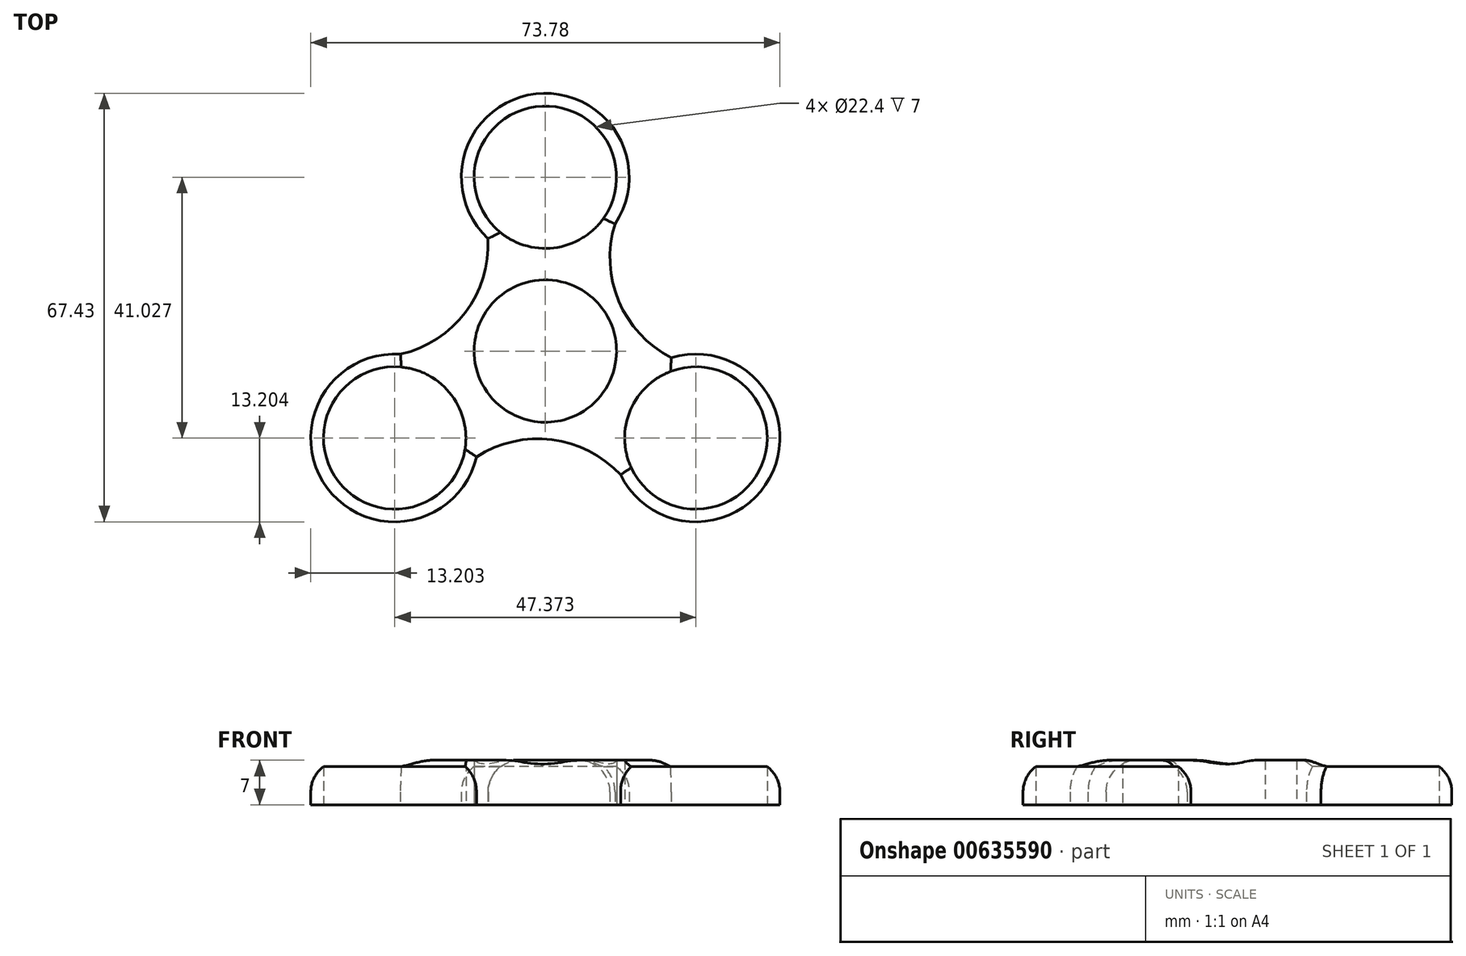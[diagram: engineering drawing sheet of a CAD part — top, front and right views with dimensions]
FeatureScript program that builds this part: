
annotation { "Feature Type Name" : "Feature", "Feature Type Description" : "" }
export const myFeature = defineFeature(function(context is Context, id is Id, definition is map)
    precondition{}
    {
        {
            var Q0;
            Q0=qCreatedBy(makeId("Top.planeOp"),FACE);
            var sketch = newSketch(context, id + "F0", { "sketchPlane" : qUnion([Q0])});
            skCircle(sketch, "E0", {"center": v(0, 0) * mm, "radius": 11.2 * mm});
            skCircle(sketch, "E1", {"center": v(0, 27.35) * mm, "radius": 11.2 * mm});
            skArc(sketch, "E2", {"start": v(10.96, 19.99) * mm, "mid": v(-1.5, 40.47) * mm, "end": v(-9, 17.7) * mm});
            skArc(sketch, "E3.1.0", {"start": v(-22.79, -0.5) * mm, "mid": v(-34.3, -21.53) * mm, "end": v(-10.83, -16.65) * mm});
            skCircle(sketch, "E3.1.1", {"center": v(-23.69, -13.68) * mm, "radius": 11.2 * mm});
            skArc(sketch, "E3.2.0", {"start": v(11.83, -19.48) * mm, "mid": v(35.8, -18.93) * mm, "end": v(19.83, -1.05) * mm});
            skCircle(sketch, "E3.2.1", {"center": v(23.69, -13.68) * mm, "radius": 11.2 * mm});
            skArc(sketch, "E4", {"start": v(10.96, 19.99) * mm, "mid": v(11.56, 7.85) * mm, "end": v(19.83, -1.05) * mm});
            skArc(sketch, "E5.1.0", {"start": v(-22.79, -0.5) * mm, "mid": v(-12.58, 6.09) * mm, "end": v(-9, 17.7) * mm});
            skArc(sketch, "E5.2.0", {"start": v(11.83, -19.48) * mm, "mid": v(1.02, -13.94) * mm, "end": v(-10.83, -16.65) * mm});
            skSolve(sketch);
        }
        {
            var Q0;
            Q0=makeQuery(id+"F0.imprint","IMPRINT",FACE,{"disambiguationData":[TD([[makeQuery(id+"F0.imprint","IMPRINT",EDGE,{"derivedFrom":sQuery(id+"F0.wireOp",EDGE,"E0")}),-1.0]])]});
            extrude(context, id + "F1", {"entities" : qUnion([Q0]), "flatOperationType" : FlatOperationType.REMOVE, "depth" : 7 * mm, "offsetDistance" : 25 * mm, "domain" : OperationDomain.MODEL});
        }
        {
            var Q0;
            Q0=makeQuery(id+"F1.opExtrude","CAP_EDGE",EDGE,{"disambiguationData":[OSD([sQuery(id+"F0.wireOp",EDGE,"E2")])],"isStart":false});
            var Q1;
            Q1=makeQuery(id+"F1.opExtrude","CAP_EDGE",EDGE,{"disambiguationData":[OSD([sQuery(id+"F0.wireOp",EDGE,"E5.1.0")])],"isStart":false});
            var Q2;
            Q2=makeQuery(id+"F1.opExtrude","CAP_EDGE",EDGE,{"disambiguationData":[OSD([sQuery(id+"F0.wireOp",EDGE,"E3.1.0")])],"isStart":false});
            var Q3;
            Q3=makeQuery(id+"F1.opExtrude","CAP_EDGE",EDGE,{"disambiguationData":[OSD([sQuery(id+"F0.wireOp",EDGE,"E5.2.0")])],"isStart":false});
            var Q4;
            Q4=makeQuery(id+"F1.opExtrude","CAP_EDGE",EDGE,{"disambiguationData":[OSD([sQuery(id+"F0.wireOp",EDGE,"E4")])],"isStart":false});
            var Q5;
            Q5=makeQuery(id+"F1.opExtrude","CAP_EDGE",EDGE,{"disambiguationData":[OSD([sQuery(id+"F0.wireOp",EDGE,"E3.2.0")])],"isStart":false});
            fillet(context, id + "F2", {"entities" : qUnion([Q0, Q1, Q2, Q3, Q4, Q5]), "radius" : 5 * mm, "tangentPropagation" : true, "defaultsChanged" : false, "allowEdgeOverflow" : false, "vertexSettings" : []});
        }
    });
